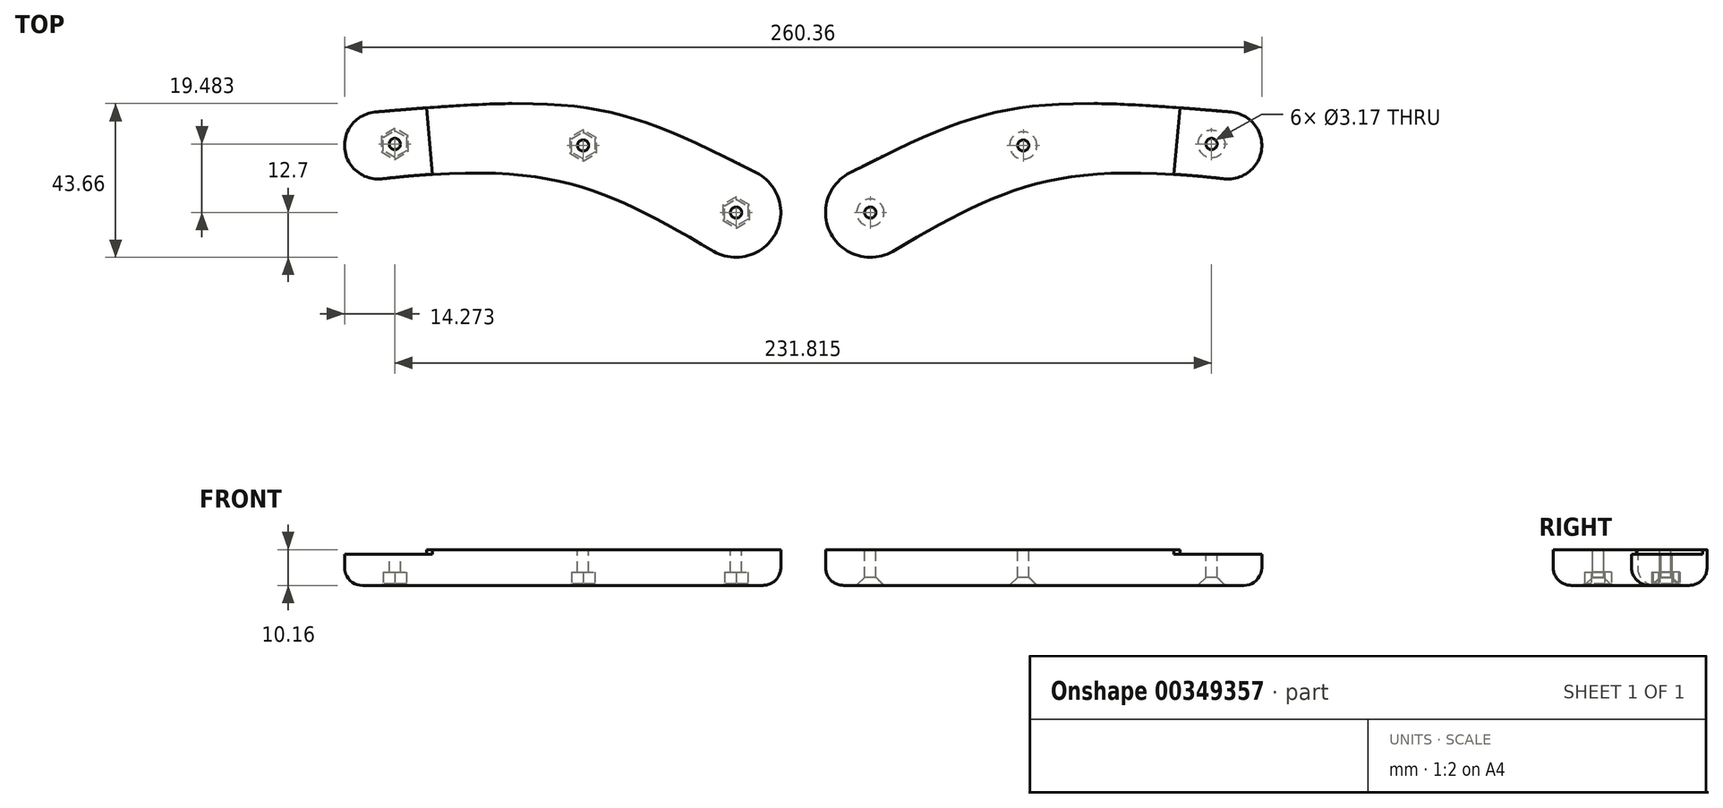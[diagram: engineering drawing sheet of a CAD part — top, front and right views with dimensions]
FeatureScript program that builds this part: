
annotation { "Feature Type Name" : "Feature", "Feature Type Description" : "" }
export const myFeature = defineFeature(function(context is Context, id is Id, definition is map)
    precondition{}
    {
        {
            var Q0;
            Q0=qCreatedBy(makeId("Top.planeOp"),FACE);
            var sketch = newSketch(context, id + "F0", { "sketchPlane" : qUnion([Q0])});
            skCircle(sketch, "E0", {"center": v(120.65, 19.05) * mm, "radius": 9.53 * mm});
            skCircle(sketch, "E1", {"center": v(19.05, 0) * mm, "radius": 12.7 * mm});
            skLineSegment(sketch, "E2.bottom", {"start": v(19.05, 0) * mm, "end": v(120.65, 0) * mm, "construction": true});
            skLineSegment(sketch, "E2.top", {"start": v(19.05, 19.05) * mm, "end": v(120.65, 19.05) * mm, "construction": true});
            skLineSegment(sketch, "E2.left", {"start": v(19.05, 0) * mm, "end": v(19.05, 19.05) * mm, "construction": true});
            skLineSegment(sketch, "E2.right", {"start": v(120.65, 0) * mm, "end": v(120.65, 19.05) * mm, "construction": true});
            skFitSpline(sketch, "E3", {"points": [v(13.29, 11.32) * mm, v(121.49, 28.54) * mm], "startDerivative": vector(119.59, 60.87) * mm, "endDerivative": vector(178.24, -15.7) * mm});
            skFitSpline(sketch, "E4", {"points": [v(119.59, 9.58) * mm, v(25.42, -10.99) * mm], "startDerivative": vector(-147.22, 16.5) * mm, "endDerivative": vector(-91.35, -52.92) * mm});
            skLineSegment(sketch, "E5", {"start": v(112.03, 29.34) * mm, "end": v(110.3, 10.5) * mm});
            skPoint(sketch, "E6", {"position": v(111.16, 19.92) * mm});
            skCircle(sketch, "E7", {"center": v(19.05, 0) * mm, "radius": 1.59 * mm});
            skCircle(sketch, "E8", {"center": v(62.47, 19.05) * mm, "radius": 1.59 * mm});
            skLineSegment(sketch, "E9", {"start": v(111.16, 19.92) * mm, "end": v(120.65, 19.05) * mm, "construction": true});
            skCircle(sketch, "E10", {"center": v(115.9, 19.48) * mm, "radius": 1.59 * mm});
            skLineSegment(sketch, "E11", {"start": v(106.95, 29.74) * mm, "end": v(105.24, 10.86) * mm});
            skSolve(sketch);
        }
        {
            var Q0;
            Q0 = qSketchRegion(id + "F0", true);
            extrude(context, id + "F1", {"entities" : qUnion([Q0]), "oppositeDirection" : true, "depth" : 10.16 * mm});
        }
        {
            var Q0;
            Q0=makeQuery(id+"F1.opExtrude","CAP_EDGE",EDGE,{"disambiguationData":[OSD([sQuery(id+"F0.wireOp",EDGE,"E4")])],"isStart":false});
            fillet(context, id + "F2", {"entities" : qUnion([Q0]), "radius" : 5.08 * mm, "tangentPropagation" : true, "allowEdgeOverflow" : false});
        }
        {
            var Q0;
            Q0=makeQuery(id+"F0.imprint","IMPRINT",FACE,{"disambiguationData":[TD([[makeQuery(id+"F0.imprint","IMPRINT",EDGE,{"derivedFrom":sQuery(id+"F0.wireOp",EDGE,"E10")}),-1.0]])]});
            var Q1;
            {var subQ0=sQuery(id+"F0.wireOp",EDGE,"E3");var subQ1=sQuery(id+"F0.wireOp",EDGE,"E0");var subQ2=makeQuery(id+"F0.imprint","INTERSECT",VERTEX,{"derivedFrom":[subQ1,subQ0]});Q1=makeQuery(id+"F0.imprint","IMPRINT",FACE,{"disambiguationData":[TD([[makeQuery(id+"F0.imprint","IMPRINT",EDGE,{"disambiguationData":[TD([[subQ2,-1.0]])],"derivedFrom":subQ1}),-1.0]])]});}
            var Q2;
            {var subQ0=sQuery(id+"F0.wireOp",EDGE,"E4");var subQ1=sQuery(id+"F0.wireOp",EDGE,"E0");var subQ2=makeQuery(id+"F0.imprint","INTERSECT",VERTEX,{"derivedFrom":[subQ1,subQ0]});Q2=makeQuery(id+"F0.imprint","IMPRINT",FACE,{"disambiguationData":[TD([[makeQuery(id+"F0.imprint","IMPRINT",EDGE,{"disambiguationData":[TD([[subQ2,1.0]])],"derivedFrom":subQ1}),-1.0]])]});}
            var Q3;
            {var subQ4=sQuery(id+"F0.wireOp",EDGE,"E11");Q3=makeQuery(id+"F0.imprint","IMPRINT",FACE,{"disambiguationData":[TD([[makeQuery(id+"F0.imprint","IMPRINT",EDGE,{"derivedFrom":subQ4}),1.0]])]});}
            extrude(context, id + "F3", {"entities" : qUnion([Q0, Q1, Q2, Q3]), "operationType" : NewBodyOperationType.REMOVE, "oppositeDirection" : true, "depth" : 1.27 * mm});
        }
        {
            var Q0;
            Q0=makeQuery(id+"F1.opExtrude","SWEPT_BODY",BODY,{"disambiguationData":[OSD([sQuery(id+"F0.wireOp",EDGE,"E0"),sQuery(id+"F0.wireOp",EDGE,"E1"),sQuery(id+"F0.wireOp",EDGE,"E3"),sQuery(id+"F0.wireOp",EDGE,"E4"),sQuery(id+"F0.wireOp",EDGE,"E7"),sQuery(id+"F0.wireOp",EDGE,"E8"),sQuery(id+"F0.wireOp",EDGE,"E10")])]});
            var Q1;
            Q1=qCreatedBy(makeId("Right.planeOp"),FACE);
            mirror(context, id + "F4", {"entities" : qUnion([Q0]), "mirrorPlane" : qUnion([Q1])});
        }
        {
            var Q0;
            Q0=makeQuery(id+"F1.opExtrude","CAP_EDGE",EDGE,{"disambiguationData":[OSD([sQuery(id+"F0.wireOp",EDGE,"E7")])],"isStart":false});
            var Q1;
            Q1=makeQuery(id+"F1.opExtrude","CAP_EDGE",EDGE,{"disambiguationData":[OSD([sQuery(id+"F0.wireOp",EDGE,"E8")])],"isStart":false});
            var Q2;
            Q2=makeQuery(id+"F1.opExtrude","CAP_EDGE",EDGE,{"disambiguationData":[OSD([sQuery(id+"F0.wireOp",EDGE,"E10")])],"isStart":false});
            chamfer(context, id + "F5", {"entities" : qUnion([Q0, Q1, Q2]), "width" : 2.3 * mm, "tangentPropagation" : true});
        }
        {
            var Q0;
            Q0=makeQuery(id+"F4.opPattern","COPY",FACE,{"derivedFrom":makeQuery(id+"F1.opExtrude","CAP_FACE",FACE,{"disambiguationData":[OSD([sQuery(id+"F0.wireOp",EDGE,"E0"),sQuery(id+"F0.wireOp",EDGE,"E1"),sQuery(id+"F0.wireOp",EDGE,"E3"),sQuery(id+"F0.wireOp",EDGE,"E4"),sQuery(id+"F0.wireOp",EDGE,"E7"),sQuery(id+"F0.wireOp",EDGE,"E8"),sQuery(id+"F0.wireOp",EDGE,"E10")])],"isStart":false}),"instanceName":"1"});
            var sketch = newSketch(context, id + "F6", { "sketchPlane" : qUnion([Q0])});
            skCircle(sketch, "E12.cCircle", {"center": v(-115.9, -19.48) * mm, "radius": 3.3 * mm, "construction": true});
            skLineSegment(sketch, "E12.0", {"start": v(-112.6, -17.58) * mm, "end": v(-112.6, -21.39) * mm});
            skLineSegment(sketch, "E12.1", {"start": v(-112.6, -21.39) * mm, "end": v(-115.9, -23.3) * mm});
            skLineSegment(sketch, "E12.2", {"start": v(-115.9, -23.3) * mm, "end": v(-119.2, -21.39) * mm});
            skLineSegment(sketch, "E12.3", {"start": v(-119.2, -21.39) * mm, "end": v(-119.2, -17.58) * mm});
            skLineSegment(sketch, "E12.4", {"start": v(-119.2, -17.58) * mm, "end": v(-115.9, -15.67) * mm});
            skLineSegment(sketch, "E12.5", {"start": v(-115.9, -15.67) * mm, "end": v(-112.6, -17.58) * mm});
            skPoint(sketch, "E12.0.midPoint", {"position": v(-112.6, -19.48) * mm});
            skCircle(sketch, "E13.cCircle", {"center": v(-62.47, -19.05) * mm, "radius": 3.3 * mm, "construction": true});
            skLineSegment(sketch, "E13.0", {"start": v(-59.16, -17.14) * mm, "end": v(-59.16, -20.96) * mm});
            skLineSegment(sketch, "E13.1", {"start": v(-59.16, -20.96) * mm, "end": v(-62.47, -22.86) * mm});
            skLineSegment(sketch, "E13.2", {"start": v(-62.47, -22.86) * mm, "end": v(-65.77, -20.96) * mm});
            skLineSegment(sketch, "E13.3", {"start": v(-65.77, -20.96) * mm, "end": v(-65.77, -17.14) * mm});
            skLineSegment(sketch, "E13.4", {"start": v(-65.77, -17.14) * mm, "end": v(-62.47, -15.24) * mm});
            skLineSegment(sketch, "E13.5", {"start": v(-62.47, -15.24) * mm, "end": v(-59.16, -17.14) * mm});
            skPoint(sketch, "E13.0.midPoint", {"position": v(-59.16, -19.05) * mm});
            skCircle(sketch, "E14.cCircle", {"center": v(-19.05, 0) * mm, "radius": 3.3 * mm, "construction": true});
            skLineSegment(sketch, "E14.0", {"start": v(-15.75, 1.9) * mm, "end": v(-15.75, -1.9) * mm});
            skLineSegment(sketch, "E14.1", {"start": v(-15.75, -1.9) * mm, "end": v(-19.05, -3.81) * mm});
            skLineSegment(sketch, "E14.2", {"start": v(-19.05, -3.81) * mm, "end": v(-22.35, -1.9) * mm});
            skLineSegment(sketch, "E14.3", {"start": v(-22.35, -1.9) * mm, "end": v(-22.35, 1.9) * mm});
            skLineSegment(sketch, "E14.4", {"start": v(-22.35, 1.9) * mm, "end": v(-19.05, 3.81) * mm});
            skLineSegment(sketch, "E14.5", {"start": v(-19.05, 3.81) * mm, "end": v(-15.75, 1.9) * mm});
            skPoint(sketch, "E14.0.midPoint", {"position": v(-15.75, 0) * mm});
            skSolve(sketch);
        }
        {
            var Q0;
            Q0=makeQuery(id+"F6.imprint","IMPRINT",FACE,{"disambiguationData":[TD([[makeQuery(id+"F6.imprint","IMPRINT",EDGE,{"derivedFrom":sQuery(id+"F6.wireOp",EDGE,"E12.0")}),-1.0]])]});
            var Q1;
            Q1=makeQuery(id+"F6.imprint","IMPRINT",FACE,{"disambiguationData":[TD([[makeQuery(id+"F6.imprint","IMPRINT",EDGE,{"derivedFrom":sQuery(id+"F6.wireOp",EDGE,"E13.0")}),-1.0]])]});
            var Q2;
            Q2=makeQuery(id+"F6.imprint","IMPRINT",FACE,{"disambiguationData":[TD([[makeQuery(id+"F6.imprint","IMPRINT",EDGE,{"derivedFrom":sQuery(id+"F6.wireOp",EDGE,"E14.0")}),-1.0]])]});
            extrude(context, id + "F7", {"entities" : qUnion([Q0, Q1, Q2]), "operationType" : NewBodyOperationType.REMOVE, "oppositeDirection" : true, "depth" : 3.8 * mm});
        }
        {
            var Q0;
            Q0=makeQuery(id+"F4.opPattern","COPY",FACE,{"derivedFrom":makeQuery(id+"F1.opExtrude","CAP_FACE",FACE,{"disambiguationData":[OSD([sQuery(id+"F0.wireOp",EDGE,"E0"),sQuery(id+"F0.wireOp",EDGE,"E1"),sQuery(id+"F0.wireOp",EDGE,"E3"),sQuery(id+"F0.wireOp",EDGE,"E4"),sQuery(id+"F0.wireOp",EDGE,"E7"),sQuery(id+"F0.wireOp",EDGE,"E8"),sQuery(id+"F0.wireOp",EDGE,"E10")])],"isStart":false}),"instanceName":"1"});
            chamfer(context, id + "F8", {"entities" : qUnion([Q0]), "width" : 0.5 * mm, "tangentPropagation" : true});
        }
    });
